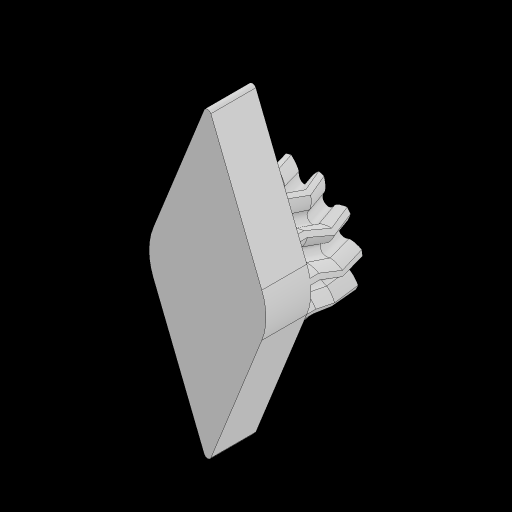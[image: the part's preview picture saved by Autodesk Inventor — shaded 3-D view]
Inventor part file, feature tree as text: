
AUTODESK INVENTOR PART (.ipt)
format: ipt  version: 2023.2 (Build 272271030, 271C)  size: 6,016,000 bytes
history: native  units: mm
features: sketch x4, extrude x4, projected_geometry x3, helix x1, pattern_circular x1, mirror x1, fillet x1
ambient origin geometry x8: Origin, YZ Plane, XZ Plane, XY Plane, X Axis, Y Axis, Z Axis, Center Point
bodies: Solid1 (feature_tree)
feature tree (15):
  sketch  "Sketch1"  dims[d0=2.5mm d1=0.0mm]
  extrude  "Extrusion1"  Depth=10.0mm TaperAngle=0.0deg
  helix  "Coil1"  [1 undecoded]
  pattern_circular  "Circular Pattern1"  [2 undecoded]
  mirror  "Mirror1"
  extrude  "Extrusion2"  [1 undecoded]
  extrude  "Extrusion3"  [1 undecoded]
  fillet  "Fillet1"  [1 undecoded]
  extrude  "Extrusion4"  [1 undecoded]
  sketch  "Sketch2"  dims[d2=110.1mm d3=10.0mm d4=10.0mm d5=0.0mm d6=90.0deg d7=90.0deg d8=0.0mm d9=0.0mm d10=110.0mm d11=360.0deg d13=1.0mm d14=0.0mm d15=35.0mm]
  projected_geometry  "Projected Loop1"
  sketch  "Sketch3"  dims[d16=5.0mm d17=0.0mm]
  projected_geometry  "Projected Loop2"
  sketch  "Sketch4"  dims[d18=0.4mm d19=0.25mm d20=0.0mm]
  projected_geometry  "Projected Loop3"
note: 7 required parameter values undecoded (feature->parameter linkage not recoverable at this tier; creation-order binding heuristic only, values carry confidence <= 0.55)
